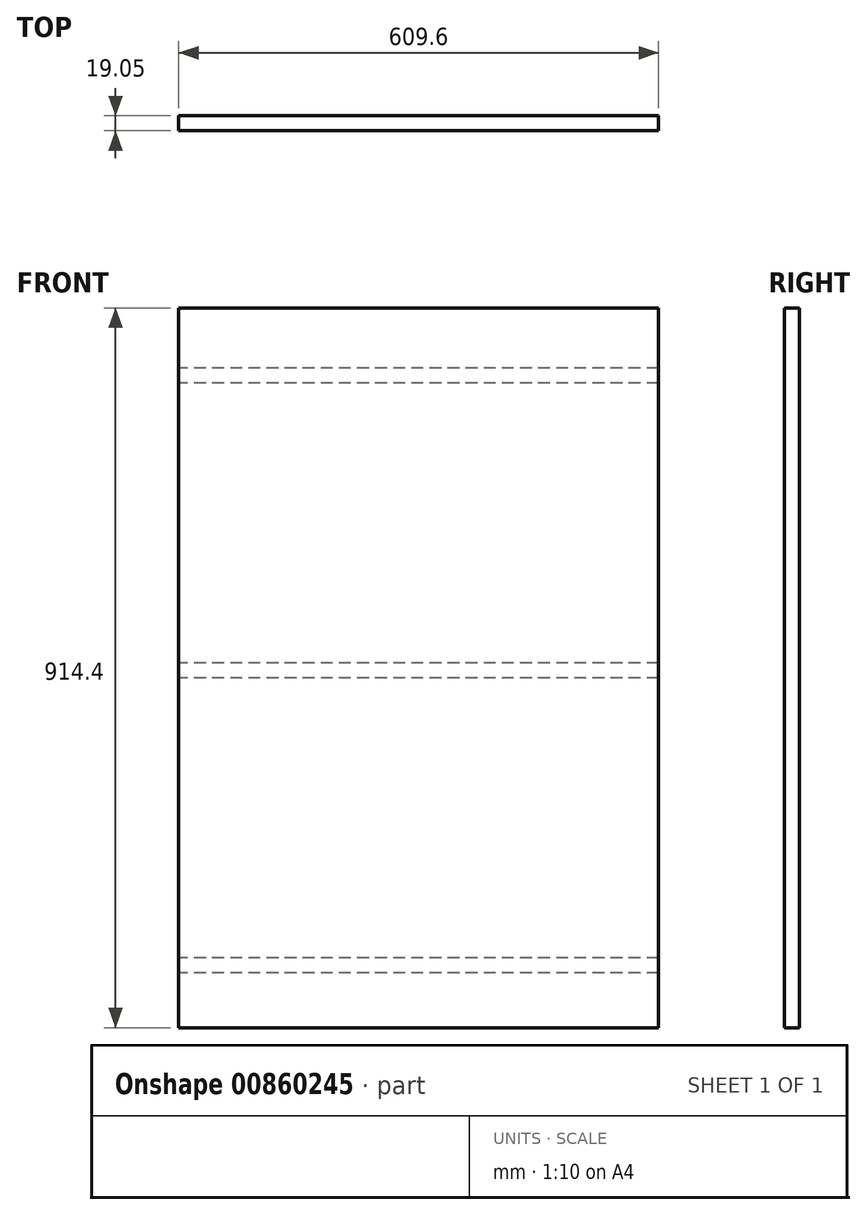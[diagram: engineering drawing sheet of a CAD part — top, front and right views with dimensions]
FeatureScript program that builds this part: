
annotation { "Feature Type Name" : "Feature", "Feature Type Description" : "" }
export const myFeature = defineFeature(function(context is Context, id is Id, definition is map)
    precondition{}
    {
        {
            var Q0;
            Q0=qCreatedBy(makeId("Front.planeOp"),FACE);
            var sketch = newSketch(context, id + "F0", { "sketchPlane" : qUnion([Q0])});
            skLineSegment(sketch, "E0.bottom", {"start": v(609.6, 914.4) * mm, "end": v(0, 914.4) * mm});
            skLineSegment(sketch, "E0.top", {"start": v(609.6, 0) * mm, "end": v(0, 0) * mm});
            skLineSegment(sketch, "E0.left", {"start": v(609.6, 914.4) * mm, "end": v(609.6, 0) * mm});
            skLineSegment(sketch, "E0.right", {"start": v(0, 914.4) * mm, "end": v(0, 0) * mm});
            skSolve(sketch);
        }
        {
            var Q0;
            Q0 = qSketchRegion(id + "F0", true);
            extrude(context, id + "F1", {"entities" : qUnion([Q0]), "depth" : 19.05 * mm, "offsetDistance" : 25 * mm});
        }
        {
            var Q0;
            Q0=makeQuery(id+"F1.opExtrude","CAP_FACE",FACE,{"disambiguationData":[OSD([sQuery(id+"F0.wireOp",EDGE,"E0.bottom"),sQuery(id+"F0.wireOp",EDGE,"E0.top"),sQuery(id+"F0.wireOp",EDGE,"E0.left"),sQuery(id+"F0.wireOp",EDGE,"E0.right")])],"isStart":true});
            var sketch = newSketch(context, id + "F2", { "sketchPlane" : qUnion([Q0])});
            skLineSegment(sketch, "E1.bottom", {"start": v(-609.6, 88.9) * mm, "end": v(0, 88.9) * mm});
            skLineSegment(sketch, "E1.top", {"start": v(-609.6, 69.85) * mm, "end": v(0, 69.85) * mm});
            skLineSegment(sketch, "E1.left", {"start": v(0, 88.9) * mm, "end": v(0, 69.85) * mm});
            skLineSegment(sketch, "E1.right", {"start": v(-609.6, 88.9) * mm, "end": v(-609.6, 69.85) * mm});
            skLineSegment(sketch, "E2.bottom", {"start": v(-609.6, 463.55) * mm, "end": v(0, 463.55) * mm});
            skLineSegment(sketch, "E2.top", {"start": v(-609.6, 444.5) * mm, "end": v(0, 444.5) * mm});
            skLineSegment(sketch, "E2.left", {"start": v(0, 463.55) * mm, "end": v(0, 444.5) * mm});
            skLineSegment(sketch, "E2.right", {"start": v(-609.6, 463.55) * mm, "end": v(-609.6, 444.5) * mm});
            skLineSegment(sketch, "E3.bottom", {"start": v(-609.6, 838.2) * mm, "end": v(0, 838.2) * mm});
            skLineSegment(sketch, "E3.top", {"start": v(-609.6, 819.15) * mm, "end": v(0, 819.15) * mm});
            skLineSegment(sketch, "E3.left", {"start": v(0, 838.2) * mm, "end": v(0, 819.15) * mm});
            skLineSegment(sketch, "E3.right", {"start": v(-609.6, 838.2) * mm, "end": v(-609.6, 819.15) * mm});
            skSolve(sketch);
        }
        {
            var Q0;
            Q0 = qSketchRegion(id + "F2", true);
            extrude(context, id + "F3", {"entities" : qUnion([Q0]), "operationType" : NewBodyOperationType.REMOVE, "oppositeDirection" : true, "depth" : 0.75 / 50.8 * mm, "offsetDistance" : 25.4 * mm});
        }
    });
